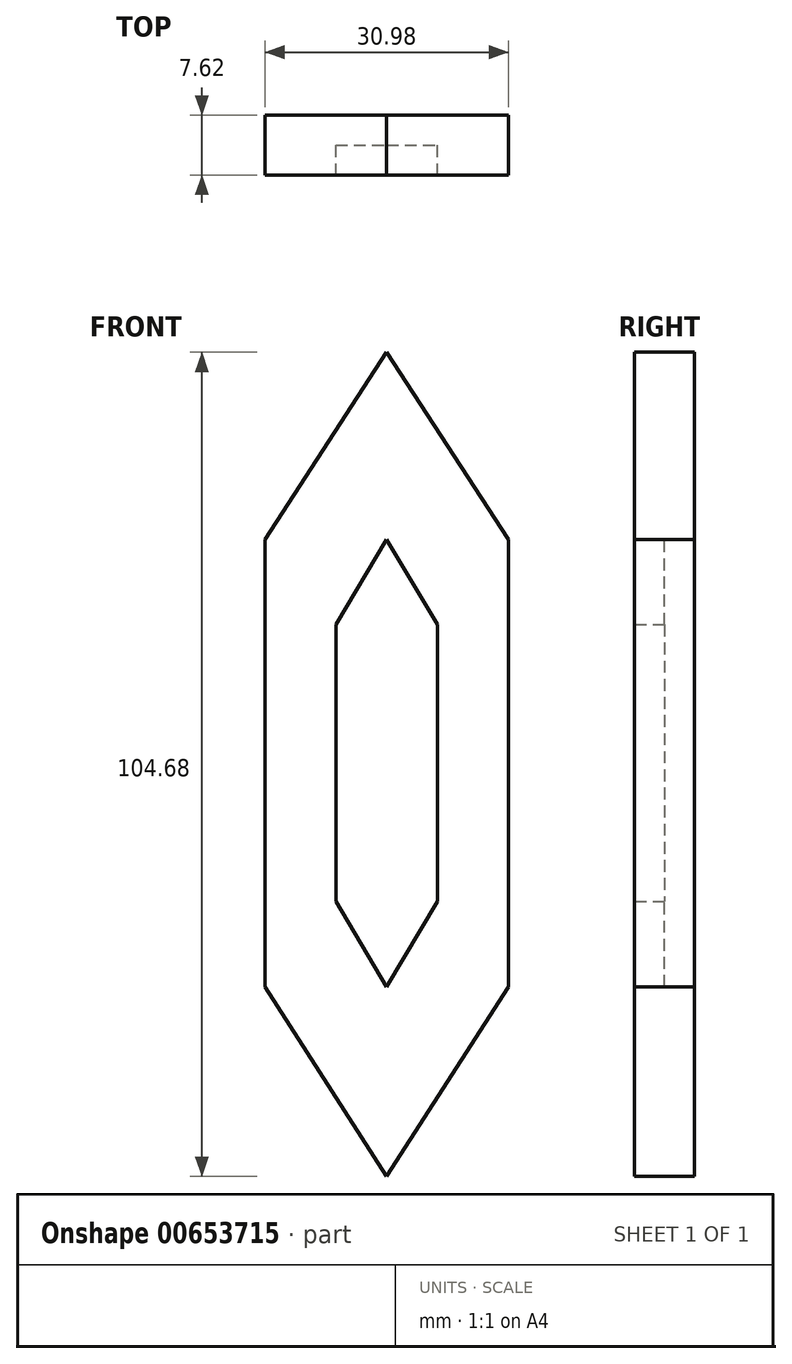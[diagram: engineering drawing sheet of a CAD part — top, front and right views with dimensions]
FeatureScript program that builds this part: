
annotation { "Feature Type Name" : "Feature", "Feature Type Description" : "" }
export const myFeature = defineFeature(function(context is Context, id is Id, definition is map)
    precondition{}
    {
        {
            var Q0;
            Q0=qCreatedBy(makeId("Front.planeOp"),FACE);
            var sketch = newSketch(context, id + "F0", { "sketchPlane" : qUnion([Q0])});
            skLineSegment(sketch, "E0.left", {"start": v(-15.5, 28.42) * mm, "end": v(-15.5, -28.42) * mm});
            skLineSegment(sketch, "E0.right", {"start": v(15.5, 28.42) * mm, "end": v(15.5, -28.42) * mm});
            skPoint(sketch, "E0.middle", {"position": v(0, 0) * mm});
            skLineSegment(sketch, "E1", {"start": v(-15.5, 28.42) * mm, "end": v(0, 52.19) * mm});
            skLineSegment(sketch, "E2", {"start": v(0, 52.19) * mm, "end": v(15.5, 28.42) * mm});
            skLineSegment(sketch, "E3", {"start": v(-15.5, -28.42) * mm, "end": v(0, -52.49) * mm});
            skLineSegment(sketch, "E4", {"start": v(0, -52.49) * mm, "end": v(15.5, -28.42) * mm});
            skLineSegment(sketch, "E5.left", {"start": v(-6.47, 17.6) * mm, "end": v(-6.47, -17.6) * mm});
            skLineSegment(sketch, "E5.right", {"start": v(6.47, 17.6) * mm, "end": v(6.47, -17.6) * mm});
            skLineSegment(sketch, "E6", {"start": v(-6.47, 17.6) * mm, "end": v(0, 28.42) * mm});
            skLineSegment(sketch, "E7", {"start": v(0, 28.42) * mm, "end": v(6.47, 17.6) * mm});
            skLineSegment(sketch, "E8", {"start": v(-6.47, -17.6) * mm, "end": v(0, -28.42) * mm});
            skLineSegment(sketch, "E9", {"start": v(0, -28.42) * mm, "end": v(6.47, -17.6) * mm});
            skSolve(sketch);
        }
        {
            var Q0;
            Q0=makeQuery(id+"F0.imprint","IMPRINT",FACE,{"disambiguationData":[TD([[makeQuery(id+"F0.imprint","IMPRINT",EDGE,{"derivedFrom":sQuery(id+"F0.wireOp",EDGE,"E0.left")}),1.0]])]});
            extrude(context, id + "F1", {"entities" : qUnion([Q0]), "depth" : 7.62 * mm, "offsetDistance" : 25.4 * mm});
        }
        {
            var Q0;
            Q0=makeQuery(id+"F0.imprint","IMPRINT",FACE,{"disambiguationData":[TD([[makeQuery(id+"F0.imprint","IMPRINT",EDGE,{"derivedFrom":sQuery(id+"F0.wireOp",EDGE,"E5.left")}),1.0]])]});
            extrude(context, id + "F2", {"entities" : qUnion([Q0]), "operationType" : NewBodyOperationType.ADD, "depth" : 3.8 * mm, "offsetDistance" : 25.4 * mm});
        }
    });
